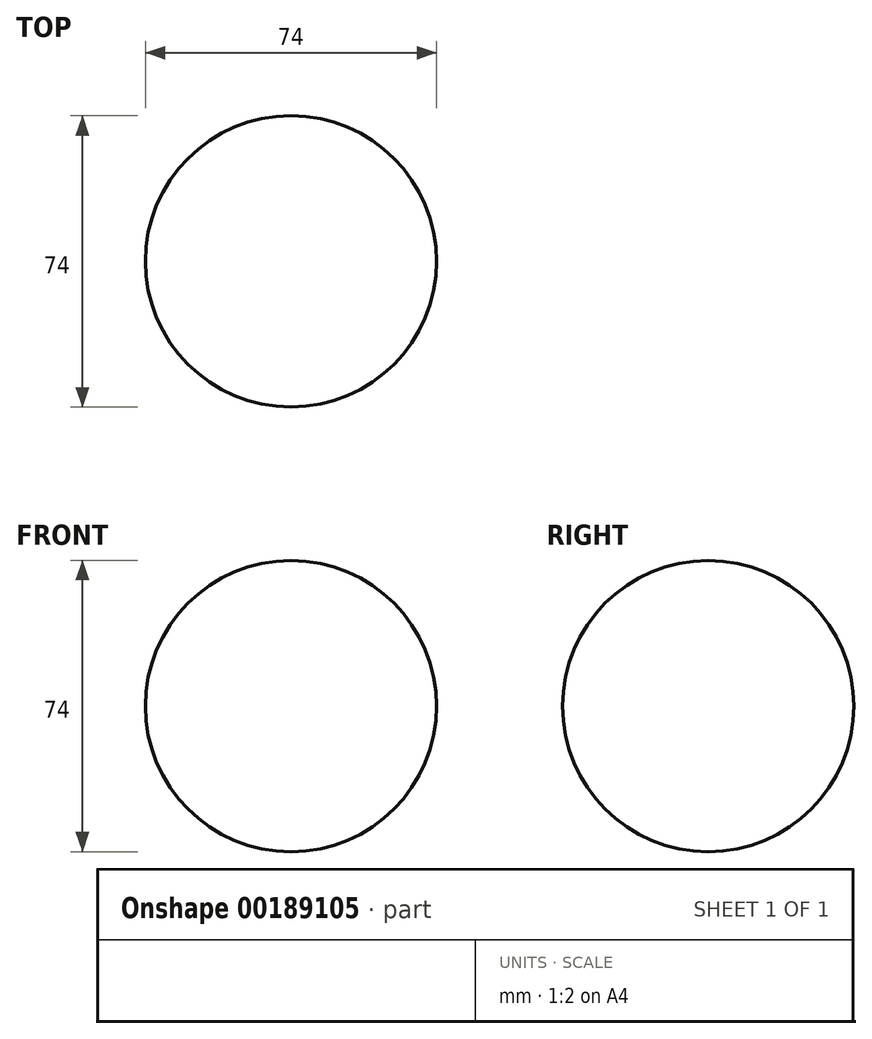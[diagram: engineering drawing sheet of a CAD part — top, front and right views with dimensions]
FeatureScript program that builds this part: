
annotation { "Feature Type Name" : "Feature", "Feature Type Description" : "" }
export const myFeature = defineFeature(function(context is Context, id is Id, definition is map)
    precondition{}
    {
        {
            var Q0;
            Q0=qCreatedBy(makeId("Front.planeOp"),FACE);
            var sketch = newSketch(context, id + "F0", { "sketchPlane" : qUnion([Q0])});
            skArc(sketch, "E0", {"start": v(0, 37) * mm, "mid": v(-37, 0) * mm, "end": v(0, -37) * mm});
            skLineSegment(sketch, "E1", {"start": v(0, 37) * mm, "end": v(0, -37) * mm});
            skSolve(sketch);
        }
        {
            var Q0;
            Q0 = qSketchRegion(id + "F0", true);
            var Q1;
            Q1=sQuery(id+"F0.wireOp",EDGE,"E1");
            revolve(context, id + "F1", {"entities" : qUnion([Q0]), "axis" : qUnion([Q1]), "revolveType" : RevolveType.FULL});
        }
    });
